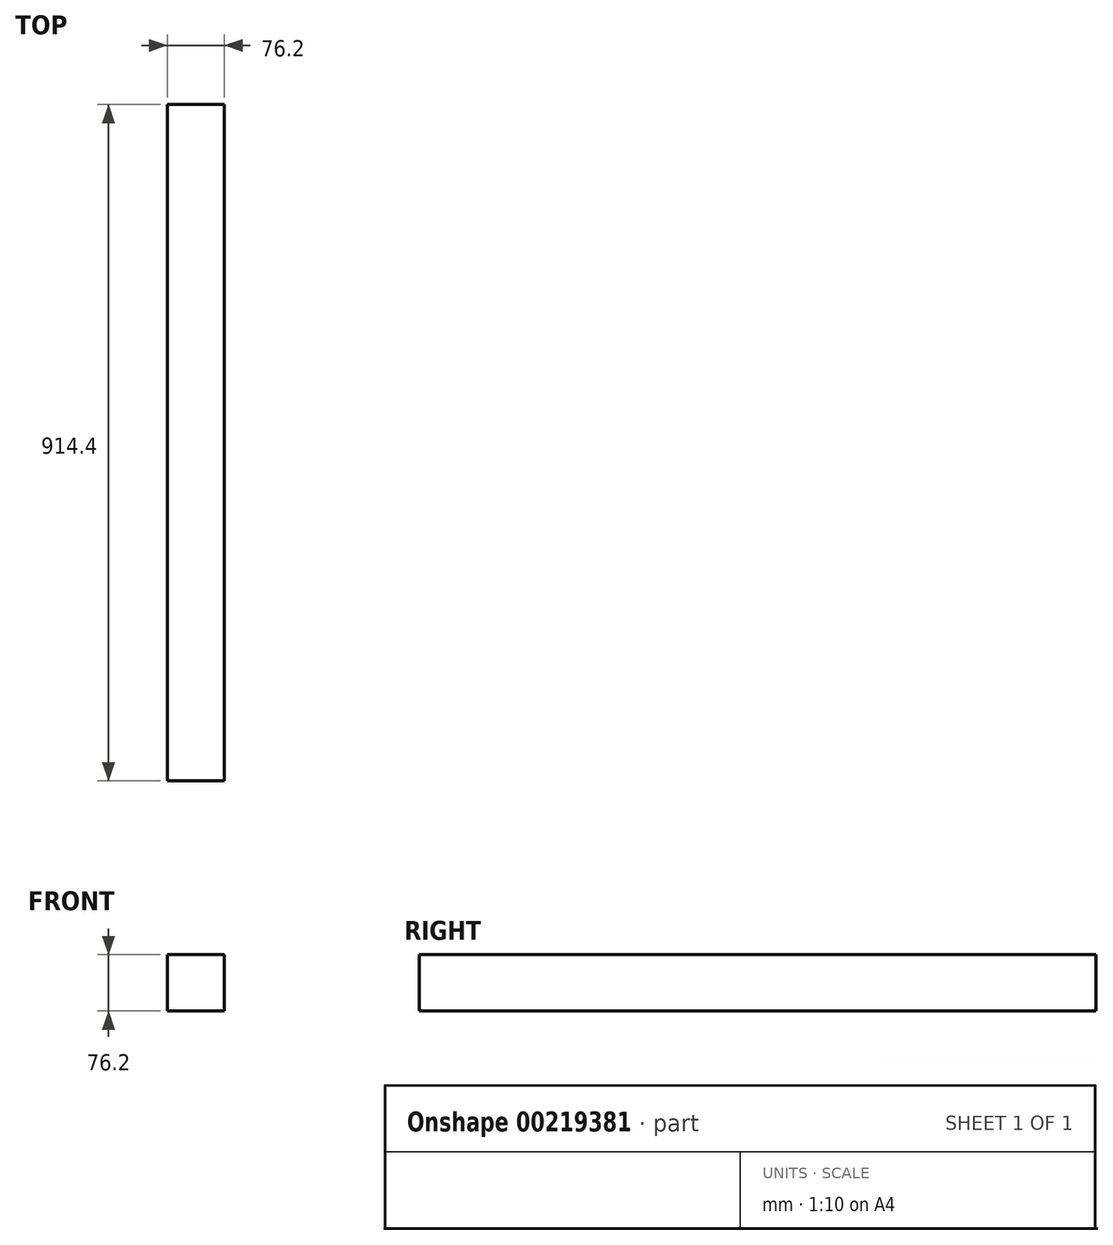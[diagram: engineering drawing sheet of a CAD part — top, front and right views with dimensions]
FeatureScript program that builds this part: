
annotation { "Feature Type Name" : "Feature", "Feature Type Description" : "" }
export const myFeature = defineFeature(function(context is Context, id is Id, definition is map)
    precondition{}
    {
        {
            var Q0;
            Q0=qCreatedBy(makeId("Front.planeOp"),FACE);
            var sketch = newSketch(context, id + "F0", { "sketchPlane" : qUnion([Q0])});
            skLineSegment(sketch, "E0.bottom", {"start": v(-38.1, 38.1) * mm, "end": v(38.1, 38.1) * mm});
            skLineSegment(sketch, "E0.top", {"start": v(-38.1, -38.1) * mm, "end": v(38.1, -38.1) * mm});
            skLineSegment(sketch, "E0.left", {"start": v(-38.1, 38.1) * mm, "end": v(-38.1, -38.1) * mm});
            skLineSegment(sketch, "E0.right", {"start": v(38.1, 38.1) * mm, "end": v(38.1, -38.1) * mm});
            skPoint(sketch, "E0.middle", {"position": v(0, 0) * mm});
            skSolve(sketch);
        }
        {
            var Q0;
            Q0 = qSketchRegion(id + "F0", true);
            extrude(context, id + "F1", {"entities" : qUnion([Q0]), "depth" : 914.4 * mm});
        }
    });
